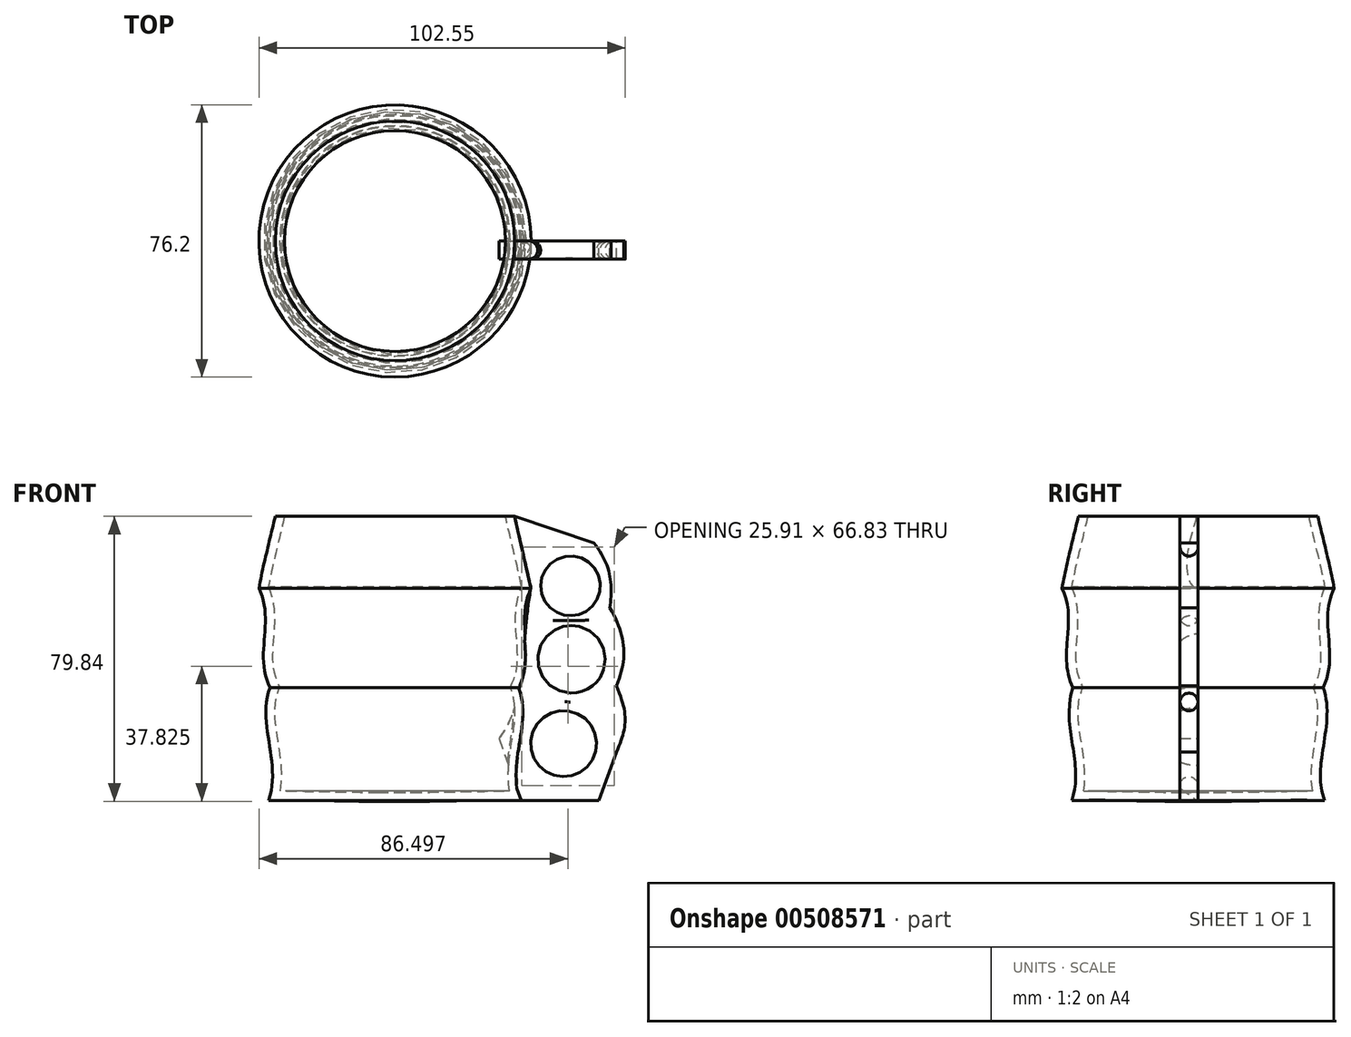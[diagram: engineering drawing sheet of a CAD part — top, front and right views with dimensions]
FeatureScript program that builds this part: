
annotation { "Feature Type Name" : "Feature", "Feature Type Description" : "" }
export const myFeature = defineFeature(function(context is Context, id is Id, definition is map)
    precondition{}
    {
        {
            var Q0;
            Q0=qCreatedBy(makeId("Front.planeOp"),FACE);
            var sketch = newSketch(context, id + "F0", { "sketchPlane" : qUnion([Q0])});
            skFitSpline(sketch, "E0", {"points": [v(0, -46.42) * mm, v(35.36, -46.18) * mm], "startDerivative": vector(35.36, -0.6) * mm, "endDerivative": vector(35.36, -0.6) * mm});
            skFitSpline(sketch, "E1", {"points": [v(35.36, -46.18) * mm, v(35.03, -14.63) * mm], "startDerivative": vector(-10.97, 31.09) * mm, "endDerivative": vector(-10.97, 31.09) * mm});
            skFitSpline(sketch, "E2", {"points": [v(35.03, -14.63) * mm, v(38.1, 13.26) * mm], "startDerivative": vector(13.72, 28.35) * mm, "endDerivative": vector(13.72, 28.35) * mm});
            skFitSpline(sketch, "E3", {"points": [v(38.1, 13.26) * mm, v(33.53, 33.38) * mm], "startDerivative": vector(-3.66, 20.12) * mm, "endDerivative": vector(-4.57, 20.12) * mm});
            skFitSpline(sketch, "E4", {"points": [v(0, -54.1) * mm, v(0, 53.8) * mm], "startDerivative": vector(0, 107.9) * mm, "endDerivative": vector(0, 107.9) * mm});
            skFitSpline(sketch, "E5", {"points": [v(33.53, 33.38) * mm, v(0, 33.38) * mm], "startDerivative": vector(-33.53, 0) * mm, "endDerivative": vector(-33.53, 0) * mm});
            skLineSegment(sketch, "E6", {"start": v(0, 58.06) * mm, "end": v(0, -67.51) * mm});
            skSolve(sketch);
        }
        {
            var Q0;
            {var subQ0=sQuery(id+"F0.wireOp",EDGE,"E0");Q0=makeQuery(id+"F0.imprint","IMPRINT",FACE,{"disambiguationData":[TD([[makeQuery(id+"F0.imprint","IMPRINT",EDGE,{"derivedFrom":subQ0}),1.0]])]});}
            var Q1;
            Q1=sQuery(id+"F0.wireOp",EDGE,"E6");
            revolve(context, id + "F1", {"entities" : qUnion([Q0]), "axis" : qUnion([Q1]), "revolveType" : RevolveType.FULL});
        }
        {
            var Q0;
            Q0=makeQuery(id+"F1.opRevolve","SWEPT_FACE",FACE,{"disambiguationData":[OSD([sQuery(id+"F0.wireOp",EDGE,"E5")])]});
            shell(context, id + "F2", {"entities" : qUnion([Q0]), "thickness" : 2.54 * mm});
        }
        {
            var Q0;
            Q0=qCreatedBy(makeId("Front.planeOp"),FACE);
            var sketch = newSketch(context, id + "F3", { "sketchPlane" : qUnion([Q0])});
            skLineSegment(sketch, "E7", {"start": v(33.52, 33.37) * mm, "end": v(55.7, 25.86) * mm});
            skFitSpline(sketch, "E8", {"points": [v(55.7, 25.86) * mm, v(60.15, 7.72) * mm], "startDerivative": vector(14.57, -17.58) * mm, "endDerivative": vector(-2.83, -18.5) * mm});
            skFitSpline(sketch, "E9", {"points": [v(60.15, 7.72) * mm, v(62, -14.1) * mm], "startDerivative": vector(13.67, -23.16) * mm, "endDerivative": vector(-9.82, -23.07) * mm});
            skFitSpline(sketch, "E10", {"points": [v(62, -14.1) * mm, v(62, -32.68) * mm], "startDerivative": vector(10.65, -24.47) * mm, "endDerivative": vector(-8.98, -20.29) * mm});
            skFitSpline(sketch, "E11", {"points": [v(29.18, -28.88) * mm, v(38.1, 13.26) * mm], "startDerivative": vector(24.89, 32.38) * mm, "endDerivative": vector(8.92, 42.14) * mm});
            skLineSegment(sketch, "E12", {"start": v(33.52, 33.37) * mm, "end": v(38.1, 13.26) * mm});
            skLineSegment(sketch, "E13", {"start": v(29.18, -28.88) * mm, "end": v(35.35, -46.18) * mm});
            skCircle(sketch, "E14", {"center": v(49.15, 13.88) * mm, "radius": 8.36 * mm});
            skCircle(sketch, "E15", {"center": v(49.43, -6.69) * mm, "radius": 9.47 * mm});
            skCircle(sketch, "E16", {"center": v(47.2, -30.32) * mm, "radius": 9.24 * mm});
            skLineSegment(sketch, "E17", {"start": v(35.35, -46.18) * mm, "end": v(57.1, -46.18) * mm});
            skLineSegment(sketch, "E18", {"start": v(57.1, -46.18) * mm, "end": v(62, -32.68) * mm});
            skSolve(sketch);
        }
        {
            var Q0;
            Q0 = qSketchRegion(id + "F3", true);
            extrude(context, id + "F4", {"entities" : qUnion([Q0]), "operationType" : NewBodyOperationType.ADD, "depth" : 5.08 * mm});
        }
        {
            var Q0;
            Q0=makeQuery(id+"F4.opExtrude","CAP_EDGE",EDGE,{"disambiguationData":[OSD([sQuery(id+"F3.wireOp",EDGE,"E14")])],"isStart":true});
            var Q1;
            Q1=makeQuery(id+"F4.opExtrude","CAP_EDGE",EDGE,{"disambiguationData":[OSD([sQuery(id+"F3.wireOp",EDGE,"E14")])],"isStart":false});
            var Q2;
            Q2=makeQuery(id+"F4.opExtrude","CAP_EDGE",EDGE,{"disambiguationData":[OSD([sQuery(id+"F3.wireOp",EDGE,"E15")])],"isStart":false});
            var Q3;
            Q3=makeQuery(id+"F4.opExtrude","CAP_EDGE",EDGE,{"disambiguationData":[OSD([sQuery(id+"F3.wireOp",EDGE,"E16")])],"isStart":false});
            var Q4;
            Q4=makeQuery(id+"F4.opExtrude","CAP_EDGE",EDGE,{"disambiguationData":[OSD([sQuery(id+"F3.wireOp",EDGE,"E15")])],"isStart":true});
            var Q5;
            Q5=makeQuery(id+"F4.opExtrude","CAP_EDGE",EDGE,{"disambiguationData":[OSD([sQuery(id+"F3.wireOp",EDGE,"E16")])],"isStart":true});
            fillet(context, id + "F5", {"entities" : qUnion([Q0, Q1, Q2, Q3, Q4, Q5]), "radius" : 2.54 * mm, "tangentPropagation" : true, "allowEdgeOverflow" : false});
        }
    });
